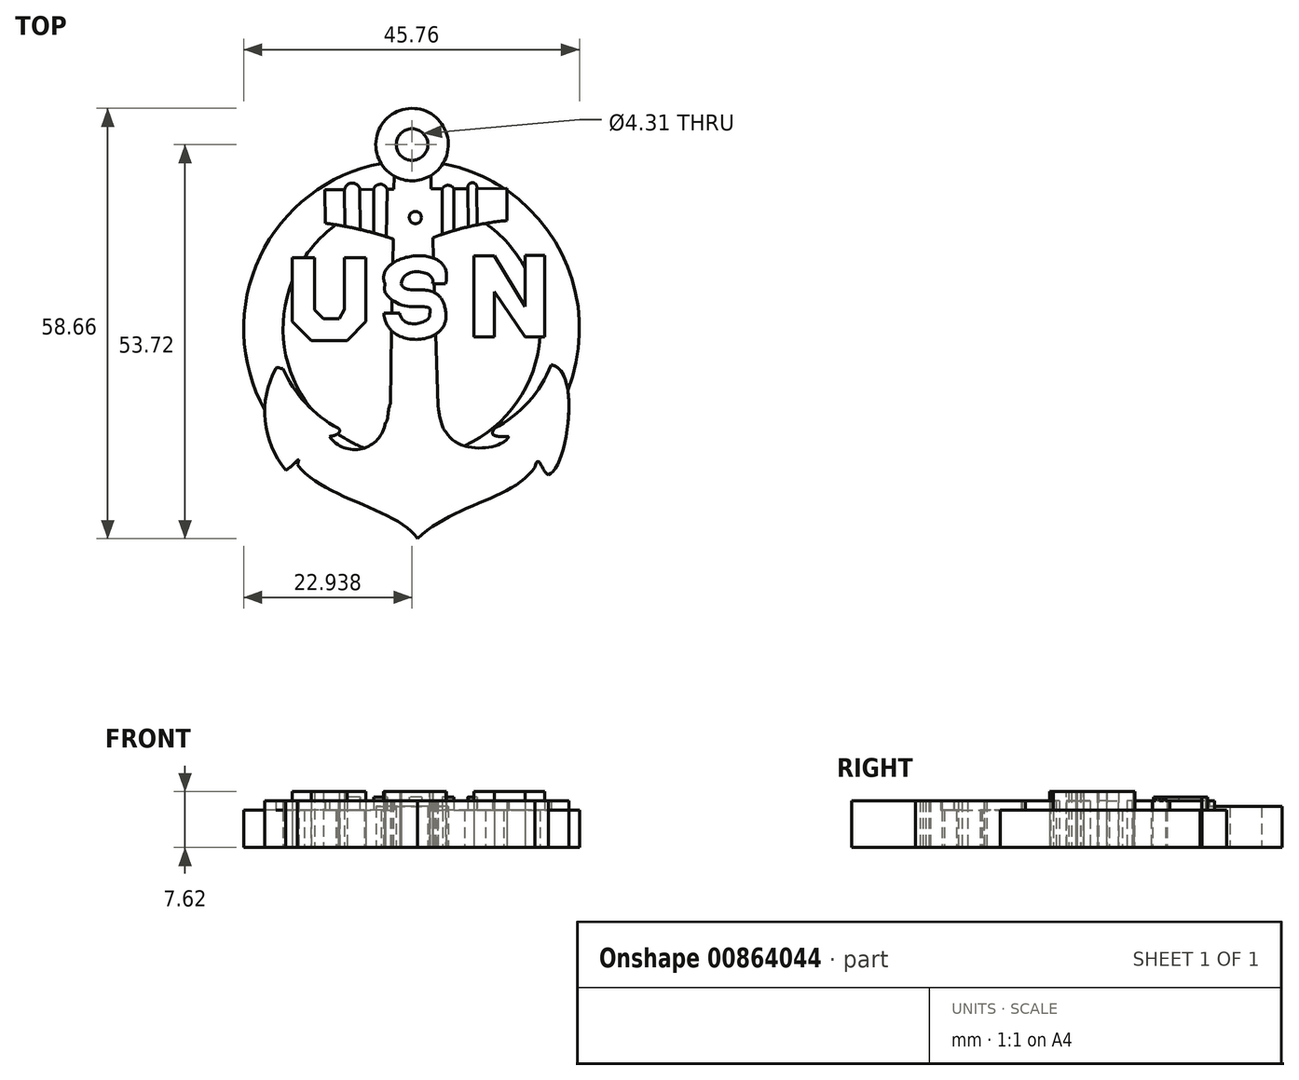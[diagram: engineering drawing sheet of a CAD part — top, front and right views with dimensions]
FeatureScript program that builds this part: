
annotation { "Feature Type Name" : "Feature", "Feature Type Description" : "" }
export const myFeature = defineFeature(function(context is Context, id is Id, definition is map)
    precondition{}
    {
        {
            var Q0;
            Q0=qCreatedBy(makeId("Top.planeOp"),FACE);
            var sketch = newSketch(context, id + "F0", { "sketchPlane" : qUnion([Q0])});
            skCircle(sketch, "E0", {"center": v(2.59, 26.22) * mm, "radius": 2.16 * mm});
            skCircle(sketch, "E1", {"center": v(2.59, 26.22) * mm, "radius": 4.94 * mm});
            skLineSegment(sketch, "E2.bottom", {"start": v(20.69, 0) * mm, "end": v(18, 0) * mm});
            skLineSegment(sketch, "E2.top", {"start": v(20.69, 11.1) * mm, "end": v(18, 11.1) * mm});
            skLineSegment(sketch, "E2.left", {"start": v(20.69, 0) * mm, "end": v(20.69, 11.1) * mm});
            skLineSegment(sketch, "E2.right", {"start": v(18, 0) * mm, "end": v(18, 11.1) * mm});
            skLineSegment(sketch, "E3.bottom", {"start": v(13.8, 0) * mm, "end": v(11.02, 0) * mm});
            skLineSegment(sketch, "E3.top", {"start": v(13.8, 11.03) * mm, "end": v(11.02, 11.03) * mm});
            skLineSegment(sketch, "E3.left", {"start": v(13.8, 0) * mm, "end": v(13.8, 11.03) * mm});
            skLineSegment(sketch, "E3.right", {"start": v(11.02, 0) * mm, "end": v(11.02, 11.03) * mm});
            skLineSegment(sketch, "E4", {"start": v(13.8, 11.03) * mm, "end": v(18, 4.14) * mm});
            skLineSegment(sketch, "E5", {"start": v(13.8, 6.15) * mm, "end": v(18, 0) * mm});
            skLineSegment(sketch, "E6", {"start": v(-13.75, 10.79) * mm, "end": v(-13.75, 2.07) * mm});
            skLineSegment(sketch, "E7", {"start": v(-13.75, 2.07) * mm, "end": v(-11.12, -0.5) * mm});
            skLineSegment(sketch, "E8", {"start": v(-11.12, -0.5) * mm, "end": v(-6.26, -0.5) * mm});
            skLineSegment(sketch, "E9", {"start": v(-6.26, -0.5) * mm, "end": v(-3.72, 2.1) * mm});
            skLineSegment(sketch, "E10", {"start": v(-3.72, 2.1) * mm, "end": v(-3.72, 10.83) * mm});
            skLineSegment(sketch, "E11", {"start": v(-3.72, 10.83) * mm, "end": v(-6.6, 10.83) * mm});
            skLineSegment(sketch, "E12", {"start": v(-6.6, 10.83) * mm, "end": v(-6.6, 3.77) * mm});
            skLineSegment(sketch, "E13", {"start": v(-6.6, 3.77) * mm, "end": v(-7.33, 2.49) * mm});
            skLineSegment(sketch, "E14", {"start": v(-7.33, 2.49) * mm, "end": v(-9.47, 2.49) * mm});
            skLineSegment(sketch, "E15", {"start": v(-9.47, 2.49) * mm, "end": v(-10.7, 3.68) * mm});
            skLineSegment(sketch, "E16", {"start": v(-10.7, 3.68) * mm, "end": v(-10.7, 10.83) * mm});
            skLineSegment(sketch, "E17", {"start": v(-10.7, 10.83) * mm, "end": v(-13.75, 10.83) * mm});
            skLineSegment(sketch, "E18", {"start": v(-13.75, 10.83) * mm, "end": v(-13.75, 10.79) * mm});
            skLineSegment(sketch, "E19", {"start": v(-9.29, 20.04) * mm, "end": v(15.5, 20.27) * mm});
            skArc(sketch, "E20", {"start": v(-4.52, 20.09) * mm, "mid": v(-5.57, 20.99) * mm, "end": v(-6.6, 20.07) * mm});
            skArc(sketch, "E21", {"start": v(-0.8, 20.12) * mm, "mid": v(-1.74, 20.81) * mm, "end": v(-2.66, 20.1) * mm});
            skArc(sketch, "E22", {"start": v(8.27, 20.2) * mm, "mid": v(7.48, 20.68) * mm, "end": v(6.7, 20.19) * mm});
            skArc(sketch, "E23", {"start": v(11.41, 20.23) * mm, "mid": v(10.8, 21.02) * mm, "end": v(10.2, 20.22) * mm});
            skLineSegment(sketch, "E24", {"start": v(5.14, 22) * mm, "end": v(6.13, -9.4) * mm});
            skLineSegment(sketch, "E25", {"start": v(0.14, 21.93) * mm, "end": v(-0.36, -9.06) * mm});
            skArc(sketch, "E26", {"start": v(13.78, -12.46) * mm, "mid": v(18.47, -8.87) * mm, "end": v(21.53, -3.82) * mm});
            skArc(sketch, "E27", {"start": v(-16, -4.28) * mm, "mid": v(-17.44, -11.42) * mm, "end": v(-14.66, -18.16) * mm});
            skArc(sketch, "E28", {"start": v(-15.02, -4.28) * mm, "mid": v(-11.94, -9) * mm, "end": v(-7.48, -12.45) * mm});
            skLineSegment(sketch, "E29", {"start": v(-9.29, 20.04) * mm, "end": v(-9.25, 15.5) * mm});
            skArc(sketch, "E30", {"start": v(2.67, 12.36) * mm, "mid": v(-3.18, 14.31) * mm, "end": v(-9.25, 15.5) * mm});
            skLineSegment(sketch, "E31", {"start": v(15.5, 20.27) * mm, "end": v(15.54, 15.86) * mm});
            skArc(sketch, "E32", {"start": v(15.54, 15.86) * mm, "mid": v(8.95, 14.68) * mm, "end": v(2.67, 12.36) * mm});
            skArc(sketch, "E33", {"start": v(-8.69, -13.55) * mm, "mid": v(-4.24, -15.24) * mm, "end": v(-1.06, -11.7) * mm});
            skFitSpline(sketch, "E34", {"points": [v(-0.36, -9.06) * mm, v(-1.06, -11.7) * mm], "startDerivative": vector(-1.38, -3.08) * mm, "endDerivative": vector(-1.4, -0.65) * mm});
            skFitSpline(sketch, "E35", {"points": [v(6.13, -9.4) * mm, v(7.23, -12.96) * mm], "startDerivative": vector(-0.02, 0.7) * mm, "endDerivative": vector(2.6, -1.78) * mm});
            skFitSpline(sketch, "E36", {"points": [v(13.78, -12.46) * mm, v(15.76, -13.56) * mm], "startDerivative": vector(-1.38, -2.73) * mm, "endDerivative": vector(6.93, 0.32) * mm});
            skFitSpline(sketch, "E37", {"points": [v(7.23, -12.96) * mm, v(15.76, -13.56) * mm], "startDerivative": vector(5.3, -9.65) * mm, "endDerivative": vector(2.09, 5.42) * mm});
            skFitSpline(sketch, "E38", {"points": [v(-13.04, -17.4) * mm, v(3.36, -27.5) * mm], "startDerivative": vector(10.93, -14.42) * mm, "endDerivative": vector(8.53, -12.5) * mm});
            skFitSpline(sketch, "E39", {"points": [v(3.36, -27.5) * mm, v(19.35, -17.76) * mm], "startDerivative": vector(14.19, 14) * mm, "endDerivative": vector(8.75, 13.08) * mm});
            skFitSpline(sketch, "E40", {"points": [v(-8.69, -13.55) * mm, v(-7.48, -12.45) * mm], "startDerivative": vector(4.67, 0.35) * mm, "endDerivative": vector(-1.18, 0.8) * mm});
            skFitSpline(sketch, "E41", {"points": [v(-14.66, -18.16) * mm, v(-13.04, -17.4) * mm], "startDerivative": vector(3.38, 1.52) * mm, "endDerivative": vector(-1.7, -4.95) * mm});
            skFitSpline(sketch, "E42", {"points": [v(19.35, -17.76) * mm, v(21.17, -18.79) * mm], "startDerivative": vector(1.4, 6.5) * mm, "endDerivative": vector(2.53, -0.66) * mm});
            skFitSpline(sketch, "E43", {"points": [v(21.17, -18.79) * mm, v(21.53, -3.82) * mm], "startDerivative": vector(7.55, 2.02) * mm, "endDerivative": vector(-12.73, 1.7) * mm});
            skFitSpline(sketch, "E44", {"points": [v(7.13, 7.22) * mm, v(-1.14, 7.29) * mm], "startDerivative": vector(4.88, 17.7) * mm, "endDerivative": vector(4.7, -12.64) * mm});
            skFitSpline(sketch, "E45", {"points": [v(-1.25, 3.21) * mm, v(7.2, 3.14) * mm], "startDerivative": vector(0.87, -14.92) * mm, "endDerivative": vector(-1.27, 13.26) * mm});
            skFitSpline(sketch, "E46", {"points": [v(0.94, 3.06) * mm, v(4.99, 3.13) * mm], "startDerivative": vector(1.63, -6.46) * mm, "endDerivative": vector(-0.65, 3.81) * mm});
            skFitSpline(sketch, "E47", {"points": [v(4.99, 3.13) * mm, v(-1.04, 5.98) * mm], "startDerivative": vector(2.03, 6.8) * mm, "endDerivative": vector(-7.77, 10.4) * mm});
            skFitSpline(sketch, "E48", {"points": [v(-1.2, 7.25) * mm, v(-1.14, 7.29) * mm, v(-1.04, 5.98) * mm], "startDerivative": vector(0.32, 0.39) * mm, "endDerivative": vector(0.81, -1.02) * mm});
            skFitSpline(sketch, "E49", {"points": [v(1.1, 7.22) * mm, v(5.37, 7.22) * mm], "startDerivative": vector(1.2, 8.3) * mm, "endDerivative": vector(-2.18, -4.98) * mm});
            skLineSegment(sketch, "E50", {"start": v(5.37, 7.22) * mm, "end": v(7.13, 7.22) * mm});
            skFitSpline(sketch, "E51", {"points": [v(1.1, 7.22) * mm, v(7.2, 3.14) * mm], "startDerivative": vector(2.3, -6.29) * mm, "endDerivative": vector(1.67, -15.96) * mm});
            skLineSegment(sketch, "E52", {"start": v(-1.25, 3.21) * mm, "end": v(0.94, 3.21) * mm});
            skFitSpline(sketch, "E53", {"points": [v(-16, -4.28) * mm, v(-15.02, -4.28) * mm], "startDerivative": vector(1.03, 1.05) * mm, "endDerivative": vector(0.59, 0.68) * mm});
            skLineSegment(sketch, "E54", {"start": v(0.94, 3.21) * mm, "end": v(0.94, 3.06) * mm});
            skCircle(sketch, "E55", {"center": v(3.04, 16.28) * mm, "radius": 0.83 * mm});
            skLineSegment(sketch, "E56", {"start": v(-6.6, 20.07) * mm, "end": v(-6.56, 15.08) * mm});
            skLineSegment(sketch, "E57", {"start": v(-4.52, 20.09) * mm, "end": v(-4.47, 14.63) * mm});
            skLineSegment(sketch, "E58", {"start": v(-2.66, 20.1) * mm, "end": v(-2.66, 14.17) * mm});
            skLineSegment(sketch, "E59", {"start": v(-0.8, 20.12) * mm, "end": v(-0.9, 13.65) * mm});
            skLineSegment(sketch, "E60", {"start": v(6.7, 20.19) * mm, "end": v(6.7, 14) * mm});
            skLineSegment(sketch, "E61", {"start": v(8.27, 20.2) * mm, "end": v(8.27, 14.5) * mm});
            skLineSegment(sketch, "E62", {"start": v(10.2, 20.22) * mm, "end": v(10.25, 15.01) * mm});
            skLineSegment(sketch, "E63", {"start": v(11.41, 20.23) * mm, "end": v(11.46, 15.28) * mm});
            skSolve(sketch);
        }
        {
            var Q0;
            Q0=qCreatedBy(makeId("Top.planeOp"),FACE);
            var sketch = newSketch(context, id + "F1", { "sketchPlane" : qUnion([Q0])});
            skCircle(sketch, "E64", {"center": v(2.53, 1.14) * mm, "radius": 17.53 * mm});
            skCircle(sketch, "E65", {"center": v(2.53, 1.14) * mm, "radius": 22.88 * mm});
            skPoint(sketch, "E66", {"position": v(2.53, 26.55) * mm});
            skSolve(sketch);
        }
        {
            var Q0;
            {var subQ4=sQuery(id+"F0.wireOp",EDGE,"E46");Q0=makeQuery(id+"F0.imprint","IMPRINT",FACE,{"disambiguationData":[TD([[makeQuery(id+"F0.imprint","IMPRINT",EDGE,{"derivedFrom":subQ4}),-1.0]])]});}
            var Q1;
            {var subQ0=sQuery(id+"F0.wireOp",EDGE,"E44");var subQ1=sQuery(id+"F0.wireOp",EDGE,"E25");var subQ2=makeQuery(id+"F0.imprint","INTERSECT",VERTEX,{"derivedFrom":[subQ1,subQ0]});Q1=makeQuery(id+"F0.imprint","IMPRINT",FACE,{"disambiguationData":[TD([[makeQuery(id+"F0.imprint","IMPRINT",EDGE,{"disambiguationData":[TD([[subQ2,-1.0]])],"derivedFrom":subQ1}),-1.0]])]});}
            var Q2;
            {var subQ0=sQuery(id+"F0.wireOp",EDGE,"E44");var subQ1=sQuery(id+"F0.wireOp",EDGE,"E24");var subQ2=makeQuery(id+"F0.imprint","INTERSECT",VERTEX,{"derivedFrom":[subQ1,subQ0]});Q2=makeQuery(id+"F0.imprint","IMPRINT",FACE,{"disambiguationData":[TD([[makeQuery(id+"F0.imprint","IMPRINT",EDGE,{"disambiguationData":[TD([[subQ2,-1.0]])],"derivedFrom":subQ1}),1.0]])]});}
            var Q3;
            {var subQ0=sQuery(id+"F0.wireOp",EDGE,"E51");var subQ1=sQuery(id+"F0.wireOp",EDGE,"E24");var subQ2=makeQuery(id+"F0.imprint","INTERSECT",VERTEX,{"derivedFrom":[subQ1,subQ0]});Q3=makeQuery(id+"F0.imprint","IMPRINT",FACE,{"disambiguationData":[TD([[makeQuery(id+"F0.imprint","IMPRINT",EDGE,{"disambiguationData":[TD([[subQ2,-1.0]])],"derivedFrom":subQ1}),1.0]])]});}
            var Q4;
            {var subQ0=sQuery(id+"F0.wireOp",EDGE,"E52");var subQ1=sQuery(id+"F0.wireOp",EDGE,"E25");var subQ2=makeQuery(id+"F0.imprint","INTERSECT",VERTEX,{"derivedFrom":[subQ1,subQ0]});Q4=makeQuery(id+"F0.imprint","IMPRINT",FACE,{"disambiguationData":[TD([[makeQuery(id+"F0.imprint","IMPRINT",EDGE,{"disambiguationData":[TD([[subQ2,-1.0]])],"derivedFrom":subQ1}),-1.0]])]});}
            var Q5;
            {var subQ3=sQuery(id+"F0.wireOp",EDGE,"E3.bottom");Q5=makeQuery(id+"F0.imprint","IMPRINT",FACE,{"disambiguationData":[TD([[makeQuery(id+"F0.imprint","IMPRINT",EDGE,{"derivedFrom":subQ3}),-1.0]])]});}
            var Q6;
            {var subQ1=sQuery(id+"F0.wireOp",EDGE,"E2.bottom");Q6=makeQuery(id+"F0.imprint","IMPRINT",FACE,{"disambiguationData":[TD([[makeQuery(id+"F0.imprint","IMPRINT",EDGE,{"derivedFrom":subQ1}),-1.0]])]});}
            var Q7;
            Q7=makeQuery(id+"F0.imprint","IMPRINT",FACE,{"disambiguationData":[TD([[makeQuery(id+"F0.imprint","IMPRINT",EDGE,{"derivedFrom":sQuery(id+"F0.wireOp",EDGE,"E6")}),1.0]])]});
            var Q8;
            {var subQ2=sQuery(id+"F0.wireOp",EDGE,"E4");Q8=makeQuery(id+"F0.imprint","IMPRINT",FACE,{"disambiguationData":[TD([[makeQuery(id+"F0.imprint","IMPRINT",EDGE,{"derivedFrom":subQ2}),-1.0]])]});}
            extrude(context, id + "F2", {"entities" : qUnion([Q0, Q1, Q2, Q3, Q4, Q5, Q6, Q7, Q8]), "depth" : 7.62 * mm, "offsetDistance" : 25.4 * mm});
        }
        {
            var Q0;
            Q0=makeQuery(id+"F0.imprint","IMPRINT",FACE,{"disambiguationData":[TD([[makeQuery(id+"F0.imprint","IMPRINT",EDGE,{"derivedFrom":sQuery(id+"F0.wireOp",EDGE,"E26")}),-1.0]])]});
            var Q1;
            {var subQ0=sQuery(id+"F0.wireOp",EDGE,"E32");var subQ3=sQuery(id+"F0.wireOp",EDGE,"E24");var subQ4=makeQuery(id+"F0.imprint","INTERSECT",VERTEX,{"derivedFrom":[subQ3,subQ0]});Q1=makeQuery(id+"F0.imprint","IMPRINT",FACE,{"disambiguationData":[TD([[makeQuery(id+"F0.imprint","IMPRINT",EDGE,{"disambiguationData":[TD([[subQ4,-1.0]])],"derivedFrom":subQ3}),-1.0]])]});}
            var Q2;
            Q2=makeQuery(id+"F0.imprint","IMPRINT",FACE,{"disambiguationData":[TD([[makeQuery(id+"F0.imprint","IMPRINT",EDGE,{"derivedFrom":sQuery(id+"F0.wireOp",EDGE,"E55")}),-1.0]])]});
            var Q3;
            {var subQ0=sQuery(id+"F0.wireOp",EDGE,"E60");Q3=makeQuery(id+"F0.imprint","IMPRINT",FACE,{"disambiguationData":[TD([[makeQuery(id+"F0.imprint","IMPRINT",EDGE,{"derivedFrom":subQ0}),-1.0]])]});}
            var Q4;
            {var subQ0=sQuery(id+"F0.wireOp",EDGE,"E59");Q4=makeQuery(id+"F0.imprint","IMPRINT",FACE,{"disambiguationData":[TD([[makeQuery(id+"F0.imprint","IMPRINT",EDGE,{"derivedFrom":subQ0}),1.0]])]});}
            var Q5;
            {var subQ0=sQuery(id+"F0.wireOp",EDGE,"E57");Q5=makeQuery(id+"F0.imprint","IMPRINT",FACE,{"disambiguationData":[TD([[makeQuery(id+"F0.imprint","IMPRINT",EDGE,{"derivedFrom":subQ0}),1.0]])]});}
            var Q6;
            {var subQ0=sQuery(id+"F0.wireOp",EDGE,"E29");Q6=makeQuery(id+"F0.imprint","IMPRINT",FACE,{"disambiguationData":[TD([[makeQuery(id+"F0.imprint","IMPRINT",EDGE,{"derivedFrom":subQ0}),1.0]])]});}
            var Q7;
            {var subQ0=sQuery(id+"F0.wireOp",EDGE,"E61");Q7=makeQuery(id+"F0.imprint","IMPRINT",FACE,{"disambiguationData":[TD([[makeQuery(id+"F0.imprint","IMPRINT",EDGE,{"derivedFrom":subQ0}),1.0]])]});}
            var Q8;
            {var subQ0=sQuery(id+"F0.wireOp",EDGE,"E31");Q8=makeQuery(id+"F0.imprint","IMPRINT",FACE,{"disambiguationData":[TD([[makeQuery(id+"F0.imprint","IMPRINT",EDGE,{"derivedFrom":subQ0}),-1.0]])]});}
            var Q9;
            {var subQ0=sQuery(id+"F0.wireOp",EDGE,"E24");var subQ1=sQuery(id+"F0.wireOp",EDGE,"E1");var subQ2=makeQuery(id+"F0.imprint","INTERSECT",VERTEX,{"derivedFrom":[subQ1,subQ0]});Q9=makeQuery(id+"F0.imprint","IMPRINT",FACE,{"disambiguationData":[TD([[makeQuery(id+"F0.imprint","IMPRINT",EDGE,{"disambiguationData":[TD([[subQ2,1.0]])],"derivedFrom":subQ1}),-1.0]])]});}
            var Q10;
            {var subQ5=sQuery(id+"F0.wireOp",EDGE,"E49");Q10=makeQuery(id+"F0.imprint","IMPRINT",FACE,{"disambiguationData":[TD([[makeQuery(id+"F0.imprint","IMPRINT",EDGE,{"derivedFrom":subQ5}),-1.0]])]});}
            var Q11;
            {var subQ1=sQuery(id+"F0.wireOp",EDGE,"E46");Q11=makeQuery(id+"F0.imprint","IMPRINT",FACE,{"disambiguationData":[TD([[makeQuery(id+"F0.imprint","IMPRINT",EDGE,{"derivedFrom":subQ1}),1.0]])]});}
            extrude(context, id + "F3", {"entities" : qUnion([Q0, Q1, Q2, Q3, Q4, Q5, Q6, Q7, Q8, Q9, Q10, Q11]), "depth" : 6.35 * mm, "offsetDistance" : 25.4 * mm});
        }
        {
            var Q0;
            {var subQ3=sQuery(id+"F0.wireOp",EDGE,"E58");Q0=makeQuery(id+"F0.imprint","IMPRINT",FACE,{"disambiguationData":[TD([[makeQuery(id+"F0.imprint","IMPRINT",EDGE,{"derivedFrom":subQ3}),1.0]])]});}
            var Q1;
            {var subQ3=sQuery(id+"F0.wireOp",EDGE,"E56");Q1=makeQuery(id+"F0.imprint","IMPRINT",FACE,{"disambiguationData":[TD([[makeQuery(id+"F0.imprint","IMPRINT",EDGE,{"derivedFrom":subQ3}),1.0]])]});}
            var Q2;
            {var subQ3=sQuery(id+"F0.wireOp",EDGE,"E60");Q2=makeQuery(id+"F0.imprint","IMPRINT",FACE,{"disambiguationData":[TD([[makeQuery(id+"F0.imprint","IMPRINT",EDGE,{"derivedFrom":subQ3}),1.0]])]});}
            var Q3;
            {var subQ3=sQuery(id+"F0.wireOp",EDGE,"E62");Q3=makeQuery(id+"F0.imprint","IMPRINT",FACE,{"disambiguationData":[TD([[makeQuery(id+"F0.imprint","IMPRINT",EDGE,{"derivedFrom":subQ3}),1.0]])]});}
            var Q4;
            {var subQ0=sQuery(id+"F0.wireOp",EDGE,"E23");Q4=makeQuery(id+"F0.imprint","IMPRINT",FACE,{"disambiguationData":[TD([[makeQuery(id+"F0.imprint","IMPRINT",EDGE,{"derivedFrom":subQ0}),1.0]])]});}
            var Q5;
            {var subQ0=sQuery(id+"F0.wireOp",EDGE,"E22");Q5=makeQuery(id+"F0.imprint","IMPRINT",FACE,{"disambiguationData":[TD([[makeQuery(id+"F0.imprint","IMPRINT",EDGE,{"derivedFrom":subQ0}),1.0]])]});}
            var Q6;
            {var subQ0=sQuery(id+"F0.wireOp",EDGE,"E21");Q6=makeQuery(id+"F0.imprint","IMPRINT",FACE,{"disambiguationData":[TD([[makeQuery(id+"F0.imprint","IMPRINT",EDGE,{"derivedFrom":subQ0}),1.0]])]});}
            var Q7;
            {var subQ0=sQuery(id+"F0.wireOp",EDGE,"E20");Q7=makeQuery(id+"F0.imprint","IMPRINT",FACE,{"disambiguationData":[TD([[makeQuery(id+"F0.imprint","IMPRINT",EDGE,{"derivedFrom":subQ0}),1.0]])]});}
            var Q8;
            Q8=makeQuery(id+"F0.imprint","IMPRINT",FACE,{"disambiguationData":[TD([[makeQuery(id+"F0.imprint","IMPRINT",EDGE,{"derivedFrom":sQuery(id+"F0.wireOp",EDGE,"E55")}),1.0]])]});
            extrude(context, id + "F4", {"entities" : qUnion([Q0, Q1, Q2, Q3, Q4, Q5, Q6, Q7, Q8]), "operationType" : NewBodyOperationType.ADD, "depth" : 6.86 * mm, "offsetDistance" : 25.4 * mm});
        }
        {
            var Q0;
            Q0=makeQuery(id+"F0.imprint","IMPRINT",FACE,{"disambiguationData":[TD([[makeQuery(id+"F0.imprint","IMPRINT",EDGE,{"derivedFrom":sQuery(id+"F0.wireOp",EDGE,"E0")}),-1.0]])]});
            extrude(context, id + "F5", {"entities" : qUnion([Q0]), "operationType" : NewBodyOperationType.ADD, "depth" : 5.6 * mm, "offsetDistance" : 25.4 * mm});
        }
        {
            var Q0;
            Q0=makeQuery(id+"F1.imprint","IMPRINT",FACE,{"disambiguationData":[TD([[makeQuery(id+"F1.imprint","IMPRINT",EDGE,{"derivedFrom":sQuery(id+"F1.wireOp",EDGE,"E64")}),-1.0]])]});
            extrude(context, id + "F6", {"entities" : qUnion([Q0]), "operationType" : NewBodyOperationType.ADD, "depth" : 5.08 * mm, "offsetDistance" : 25.4 * mm});
        }
    });
